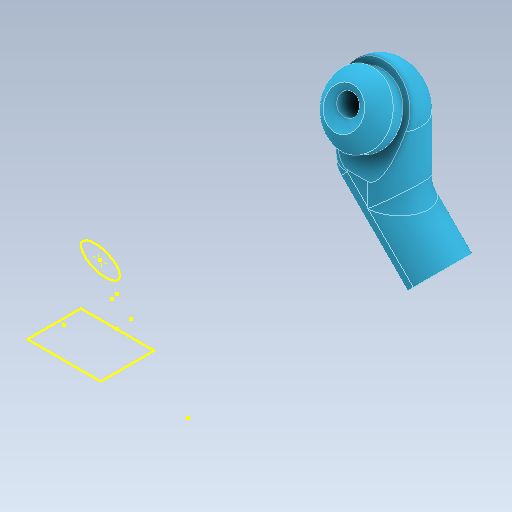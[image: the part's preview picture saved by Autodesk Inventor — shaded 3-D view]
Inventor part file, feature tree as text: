
AUTODESK INVENTOR PART (.ipt)
format: ipt  version: 2021 (Build 250183000, 183)  size: 388,096 bytes
history: native  units: mm
features: sketch x14, delete_face x6, other x4, extrude x3, mirror x2
ambient origin geometry x8: Origin, YZ Plane, XZ Plane, XY Plane, X Axis, Y Axis, Z Axis, Center Point
bodies: Solid1 (feature_tree), Solid2 (feature_tree)
feature tree (29):
  other  "toy hand part.ipt"
  sketch  "Sketch18"
  sketch  "Sketch19"
  extrude  "Extrusion1"  Depth=3.0mm
  extrude  "Extrusion2"  Depth=3.0mm
  extrude  "Extrusion3"  Depth=10.0mm
  delete_face  "Delete Face1"
  delete_face  "Delete Face2"
  delete_face  "Delete Face3"
  mirror  "Mirror1"
  delete_face  "Delete Face4"
  delete_face  "Delete Face5"
  delete_face  "Delete Face6"
  mirror  "Mirror2"
  other  "Solid2::toy hand part.ipt"
  other  "Solid3::toy hand part.ipt"
  other  "TaggingFeature1"
  sketch  "Sketch2"  dims[d0=30.0mm d1=3.0mm]
  sketch  "Sketch3"  dims[d2=3.0mm d3=3.0mm]
  sketch  "Sketch5"  dims[d4=10.0mm d5=0.698132mm d6=10.0mm d7=0.698132mm]
  sketch  "Sketch6"  dims[d8=3.0mm]
  sketch  "Sketch9"  dims[d9=7.5mm d10=0.698132mm]
  sketch  "Sketch15"
  sketch  "Sketch16"
  sketch  "Sketch17"
  sketch  "Sketch22"
  sketch  "Sketch25"
  sketch  "Sketch26"
  sketch  "Sketch20"
